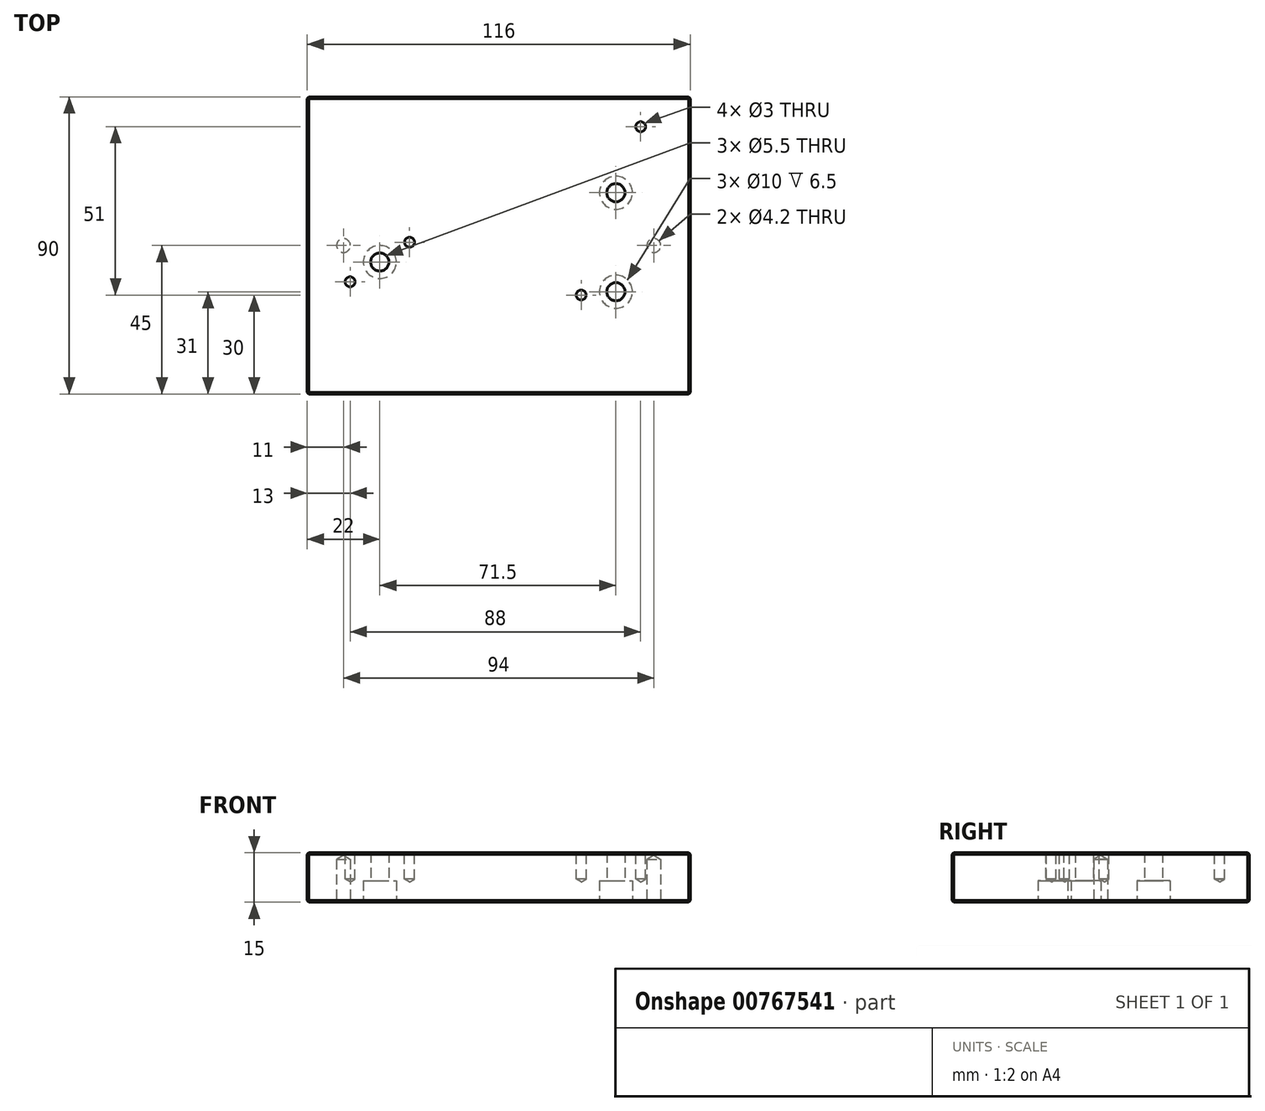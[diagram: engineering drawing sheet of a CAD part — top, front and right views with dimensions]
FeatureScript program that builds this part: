
annotation { "Feature Type Name" : "Feature", "Feature Type Description" : "" }
export const myFeature = defineFeature(function(context is Context, id is Id, definition is map)
    precondition{}
    {
        {
            var Q0;
            Q0=qCreatedBy(makeId("Top.planeOp"),FACE);
            var sketch = newSketch(context, id + "F0", { "sketchPlane" : qUnion([Q0])});
            skLineSegment(sketch, "E0.bottom", {"start": v(0, 0) * mm, "end": v(116, 0) * mm});
            skLineSegment(sketch, "E0.top", {"start": v(0, 90) * mm, "end": v(116, 90) * mm});
            skLineSegment(sketch, "E0.left", {"start": v(0, 0) * mm, "end": v(0, 90) * mm});
            skLineSegment(sketch, "E0.right", {"start": v(116, 0) * mm, "end": v(116, 90) * mm});
            skSolve(sketch);
        }
        {
            var Q0;
            Q0 = qSketchRegion(id + "F0", true);
            extrude(context, id + "F1", {"entities" : qUnion([Q0]), "depth" : 15 * mm, "offsetDistance" : 25 * mm});
        }
        {
            var Q0;
            Q0=makeQuery(id+"F1.opExtrude","CAP_FACE",FACE,{"disambiguationData":[OSD([sQuery(id+"F0.wireOp",EDGE,"E0.bottom"),sQuery(id+"F0.wireOp",EDGE,"E0.top"),sQuery(id+"F0.wireOp",EDGE,"E0.left"),sQuery(id+"F0.wireOp",EDGE,"E0.right")])],"isStart":false});
            var Q1;
            Q1=makeQuery(id+"F1.opExtrude","CAP_FACE",FACE,{"disambiguationData":[OSD([sQuery(id+"F0.wireOp",EDGE,"E0.bottom"),sQuery(id+"F0.wireOp",EDGE,"E0.top"),sQuery(id+"F0.wireOp",EDGE,"E0.left"),sQuery(id+"F0.wireOp",EDGE,"E0.right")])],"isStart":true});
            var Q2;
            Q2=makeQuery(id+"F1.opExtrude","SWEPT_FACE",FACE,{"disambiguationData":[OSD([sQuery(id+"F0.wireOp",EDGE,"E0.bottom")])]});
            var Q3;
            Q3=makeQuery(id+"F1.opExtrude","SWEPT_FACE",FACE,{"disambiguationData":[OSD([sQuery(id+"F0.wireOp",EDGE,"E0.right")])]});
            var Q4;
            Q4=makeQuery(id+"F1.opExtrude","SWEPT_FACE",FACE,{"disambiguationData":[OSD([sQuery(id+"F0.wireOp",EDGE,"E0.left")])]});
            var Q5;
            Q5=makeQuery(id+"F1.opExtrude","SWEPT_FACE",FACE,{"disambiguationData":[OSD([sQuery(id+"F0.wireOp",EDGE,"E0.top")])]});
            chamfer(context, id + "F2", {"entities" : qUnion([Q0, Q1, Q2, Q3, Q4, Q5]), "width" : 0.5 * mm, "tangentPropagation" : true});
        }
        {
            var Q0;
            Q0=makeQuery(id+"F1.opExtrude","CAP_FACE",FACE,{"disambiguationData":[OSD([sQuery(id+"F0.wireOp",EDGE,"E0.bottom"),sQuery(id+"F0.wireOp",EDGE,"E0.top"),sQuery(id+"F0.wireOp",EDGE,"E0.left"),sQuery(id+"F0.wireOp",EDGE,"E0.right")])],"isStart":false});
            var sketch = newSketch(context, id + "F3", { "sketchPlane" : qUnion([Q0])});
            skPoint(sketch, "E1", {"position": v(13, 34) * mm});
            skPoint(sketch, "E2", {"position": v(31, 46) * mm});
            skPoint(sketch, "E3", {"position": v(83, 30) * mm});
            skPoint(sketch, "E4", {"position": v(101, 81) * mm});
            skSolve(sketch);
        }
        {
            var Q0;
            Q0=qCreatedBy(makeId("Top.planeOp"),FACE);
            var sketch = newSketch(context, id + "F4", { "sketchPlane" : qUnion([Q0])});
            skPoint(sketch, "E5", {"position": v(93.5, 61) * mm});
            skPoint(sketch, "E6", {"position": v(93.5, 31) * mm});
            skPoint(sketch, "E7", {"position": v(105, 45) * mm});
            skPoint(sketch, "E8", {"position": v(22, 40) * mm});
            skPoint(sketch, "E9", {"position": v(11, 45) * mm});
            skLineSegment(sketch, "E10", {"start": v(93.5, 61) * mm, "end": v(93.5, 31) * mm, "construction": true});
            skLineSegment(sketch, "E11", {"start": v(105, 45) * mm, "end": v(11, 45) * mm, "construction": true});
            skSolve(sketch);
        }
        {
            var Q0;
            Q0=sQuery(id+"F3.wireOp",VERTEX,"E4");
            var Q1;
            Q1=sQuery(id+"F3.wireOp",VERTEX,"E2");
            var Q2;
            Q2=sQuery(id+"F3.wireOp",VERTEX,"E1");
            var Q3;
            Q3=sQuery(id+"F3.wireOp",VERTEX,"E3");
            var Q4;
            Q4=makeQuery(id+"F1.opExtrude","SWEPT_BODY",BODY,{"disambiguationData":[OSD([sQuery(id+"F0.wireOp",EDGE,"E0.bottom"),sQuery(id+"F0.wireOp",EDGE,"E0.top"),sQuery(id+"F0.wireOp",EDGE,"E0.left"),sQuery(id+"F0.wireOp",EDGE,"E0.right")])]});
            hole(context, id + "F5", {"style" : HoleStyle.SIMPLE, "endStyle" : HoleEndStyle.BLIND, "holeDiameter" : 3 * mm, "majorDiameter" : 4 * mm, "holeDepth" : 8 * mm, "tappedDepth" : 5.5 * mm, "tapClearance" : 5, "startFromSketch" : true, "locations" : qUnion([Q0, Q1, Q2, Q3]), "scope" : qUnion([Q4])});
        }
        {
            var Q0;
            Q0=sQuery(id+"F4.wireOp",VERTEX,"E7");
            var Q1;
            Q1=sQuery(id+"F4.wireOp",VERTEX,"E9");
            var Q2;
            Q2=makeQuery(id+"F1.opExtrude","SWEPT_BODY",BODY,{"disambiguationData":[OSD([sQuery(id+"F0.wireOp",EDGE,"E0.bottom"),sQuery(id+"F0.wireOp",EDGE,"E0.top"),sQuery(id+"F0.wireOp",EDGE,"E0.left"),sQuery(id+"F0.wireOp",EDGE,"E0.right")])]});
            hole(context, id + "F6", {"style" : HoleStyle.SIMPLE, "endStyle" : HoleEndStyle.BLIND, "oppositeDirection" : true, "standardTappedOrClearance" : lookupTablePath({ "standard" : "ISO", "engagement" : "75%", "pitch" : "0.8 mm", "size" : "M5", "type" : "Tapped" }), "standardBlindInLast" : lookupTablePath({ "standard" : "ISO", "engagement" : "75%", "pitch" : "0.8 mm", "size" : "M5", "type" : "Tapped" }), "holeDiameter" : 4.2 * mm, "majorDiameter" : 5 * mm, "showTappedDepth" : true, "holeDepth" : 13 * mm, "tappedDepth" : 9.8 * mm, "tapClearance" : 4, "startFromSketch" : true, "locations" : qUnion([Q0, Q1]), "scope" : qUnion([Q2])});
        }
        {
            var Q0;
            Q0=sQuery(id+"F4.wireOp",VERTEX,"E5");
            var Q1;
            Q1=sQuery(id+"F4.wireOp",VERTEX,"E6");
            var Q2;
            Q2=sQuery(id+"F4.wireOp",VERTEX,"E8");
            var Q3;
            Q3=makeQuery(id+"F1.opExtrude","SWEPT_BODY",BODY,{"disambiguationData":[OSD([sQuery(id+"F0.wireOp",EDGE,"E0.bottom"),sQuery(id+"F0.wireOp",EDGE,"E0.top"),sQuery(id+"F0.wireOp",EDGE,"E0.left"),sQuery(id+"F0.wireOp",EDGE,"E0.right")])]});
            hole(context, id + "F7", {"style" : HoleStyle.C_BORE, "endStyle" : HoleEndStyle.THROUGH, "oppositeDirection" : true, "holeDiameter" : 5.5 * mm, "cBoreDiameter" : 10 * mm, "cBoreDepth" : 6.5 * mm, "majorDiameter" : 5 * mm, "tappedDepth" : 9.8 * mm, "tapClearance" : 4, "startFromSketch" : true, "locations" : qUnion([Q0, Q1, Q2]), "scope" : qUnion([Q3])});
        }
    });
